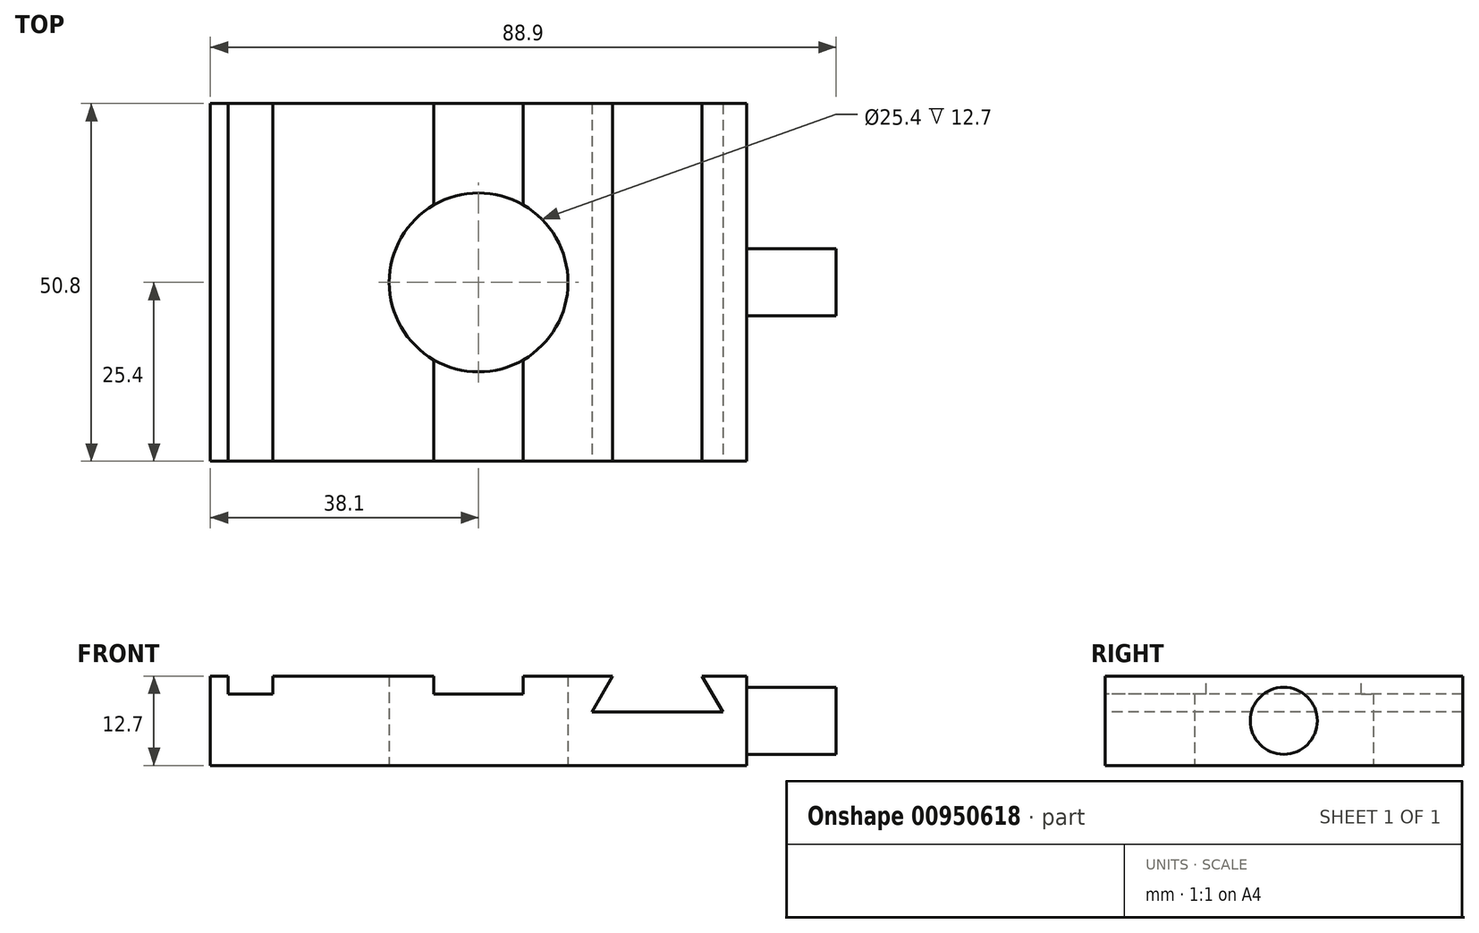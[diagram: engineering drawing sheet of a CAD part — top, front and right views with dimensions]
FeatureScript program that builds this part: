
annotation { "Feature Type Name" : "Feature", "Feature Type Description" : "" }
export const myFeature = defineFeature(function(context is Context, id is Id, definition is map)
    precondition{}
    {
        {
            var Q0;
            Q0=qCreatedBy(makeId("Top.planeOp"),FACE);
            var sketch = newSketch(context, id + "F0", { "sketchPlane" : qUnion([Q0])});
            skLineSegment(sketch, "E0.bottom", {"start": v(38.1, -25.4) * mm, "end": v(-38.1, -25.4) * mm});
            skLineSegment(sketch, "E0.top", {"start": v(38.1, 25.4) * mm, "end": v(-38.1, 25.4) * mm});
            skLineSegment(sketch, "E0.left", {"start": v(38.1, -25.4) * mm, "end": v(38.1, 25.4) * mm});
            skLineSegment(sketch, "E0.right", {"start": v(-38.1, -25.4) * mm, "end": v(-38.1, 25.4) * mm});
            skPoint(sketch, "E0.middle", {"position": v(0, 0) * mm});
            skCircle(sketch, "E1", {"center": v(0, 0) * mm, "radius": 12.7 * mm});
            skSolve(sketch);
        }
        {
            var Q0;
            Q0=makeQuery(id+"F0.imprint","IMPRINT",FACE,{"disambiguationData":[TD([[makeQuery(id+"F0.imprint","IMPRINT",EDGE,{"derivedFrom":sQuery(id+"F0.wireOp",EDGE,"E0.bottom")}),-1.0]])]});
            extrude(context, id + "F1", {"entities" : qUnion([Q0]), "depth" : 12.7 * mm, "offsetDistance" : 25.4 * mm});
        }
        {
            var Q0;
            Q0=makeQuery(id+"F1.opExtrude","CAP_FACE",FACE,{"disambiguationData":[OSD([sQuery(id+"F0.wireOp",EDGE,"E0.bottom"),sQuery(id+"F0.wireOp",EDGE,"E0.top"),sQuery(id+"F0.wireOp",EDGE,"E0.left"),sQuery(id+"F0.wireOp",EDGE,"E0.right"),sQuery(id+"F0.wireOp",EDGE,"E1")])],"isStart":false});
            var sketch = newSketch(context, id + "F2", { "sketchPlane" : qUnion([Q0])});
            skLineSegment(sketch, "E2.bottom", {"start": v(-35.56, 25.4) * mm, "end": v(-29.21, 25.4) * mm});
            skLineSegment(sketch, "E2.top", {"start": v(-35.56, -25.4) * mm, "end": v(-29.21, -25.4) * mm});
            skLineSegment(sketch, "E2.left", {"start": v(-35.56, 25.4) * mm, "end": v(-35.56, -25.4) * mm});
            skLineSegment(sketch, "E2.right", {"start": v(-29.21, 25.4) * mm, "end": v(-29.21, -25.4) * mm});
            skLineSegment(sketch, "E3", {"start": v(-6.35, 25.4) * mm, "end": v(-6.35, -25.4) * mm});
            skLineSegment(sketch, "E4", {"start": v(-6.35, -25.4) * mm, "end": v(6.35, -25.4) * mm});
            skLineSegment(sketch, "E5", {"start": v(6.35, -25.4) * mm, "end": v(6.35, 25.4) * mm});
            skPoint(sketch, "E6", {"position": v(0, 0) * mm});
            skLineSegment(sketch, "E7", {"start": v(6.35, 25.4) * mm, "end": v(-6.35, 25.4) * mm});
            skLineSegment(sketch, "E8", {"start": v(0, 25.4) * mm, "end": v(0, -25.4) * mm, "construction": true});
            skSolve(sketch);
        }
        {
            var Q0;
            Q0=makeQuery(id+"F2.imprint","IMPRINT",FACE,{"disambiguationData":[TD([[makeQuery(id+"F2.imprint","IMPRINT",EDGE,{"derivedFrom":sQuery(id+"F2.wireOp",EDGE,"E2.bottom")}),1.0]])]});
            var Q1;
            {var subQ0=sQuery(id+"F2.wireOp",EDGE,"E7");Q1=makeQuery(id+"F2.imprint","IMPRINT",FACE,{"disambiguationData":[TD([[makeQuery(id+"F2.imprint","IMPRINT",EDGE,{"derivedFrom":subQ0}),1.0]])]});}
            var Q2;
            {var subQ0=sQuery(id+"F2.wireOp",EDGE,"E4");Q2=makeQuery(id+"F2.imprint","IMPRINT",FACE,{"disambiguationData":[TD([[makeQuery(id+"F2.imprint","IMPRINT",EDGE,{"derivedFrom":subQ0}),-1.0]])]});}
            extrude(context, id + "F3", {"entities" : qUnion([Q0, Q1, Q2]), "operationType" : NewBodyOperationType.REMOVE, "oppositeDirection" : true, "depth" : 2.54 * mm, "offsetDistance" : 25.4 * mm});
        }
        {
            var Q0;
            Q0=makeQuery(id+"F1.opExtrude","SWEPT_FACE",FACE,{"disambiguationData":[OSD([sQuery(id+"F0.wireOp",EDGE,"E0.bottom")])]});
            var sketch = newSketch(context, id + "F4", { "sketchPlane" : qUnion([Q0])});
            skLineSegment(sketch, "E9", {"start": v(19.05, 12.7) * mm, "end": v(16.12, 7.62) * mm});
            skLineSegment(sketch, "E10", {"start": v(16.12, 7.62) * mm, "end": v(34.68, 7.62) * mm});
            skLineSegment(sketch, "E11", {"start": v(34.68, 7.62) * mm, "end": v(31.75, 12.7) * mm});
            skLineSegment(sketch, "E12", {"start": v(31.75, 12.7) * mm, "end": v(19.05, 12.7) * mm});
            skLineSegment(sketch, "E13", {"start": v(25.4, 12.7) * mm, "end": v(25.4, 7.62) * mm, "construction": true});
            skSolve(sketch);
        }
        {
            var Q0;
            Q0=makeQuery(id+"F4.imprint","IMPRINT",FACE,{"disambiguationData":[TD([[makeQuery(id+"F4.imprint","IMPRINT",EDGE,{"derivedFrom":sQuery(id+"F4.wireOp",EDGE,"E9")}),1.0]])]});
            extrude(context, id + "F5", {"entities" : qUnion([Q0]), "operationType" : NewBodyOperationType.REMOVE, "endBound" : BoundingType.THROUGH_ALL, "oppositeDirection" : true, "depth" : 29.46 * mm, "offsetDistance" : 25.4 * mm});
        }
        {
            var Q0;
            Q0=makeQuery(id+"F1.opExtrude","SWEPT_FACE",FACE,{"disambiguationData":[OSD([sQuery(id+"F0.wireOp",EDGE,"E0.left")])]});
            var sketch = newSketch(context, id + "F6", { "sketchPlane" : qUnion([Q0])});
            skCircle(sketch, "E14", {"center": v(0, 6.35) * mm, "radius": 4.76 * mm});
            skPoint(sketch, "E14.centerSnap0", {"position": v(-25.4, 6.35) * mm});
            skPoint(sketch, "E14.centerSnap1", {"position": v(0, 12.7) * mm});
            skSolve(sketch);
        }
        {
            var Q0;
            Q0=makeQuery(id+"F6.imprint","IMPRINT",FACE,{"disambiguationData":[TD([[makeQuery(id+"F6.imprint","IMPRINT",EDGE,{"derivedFrom":sQuery(id+"F6.wireOp",EDGE,"E14")}),1.0]])]});
            extrude(context, id + "F7", {"entities" : qUnion([Q0]), "operationType" : NewBodyOperationType.ADD, "depth" : 12.7 * mm, "offsetDistance" : 25.4 * mm});
        }
    });
